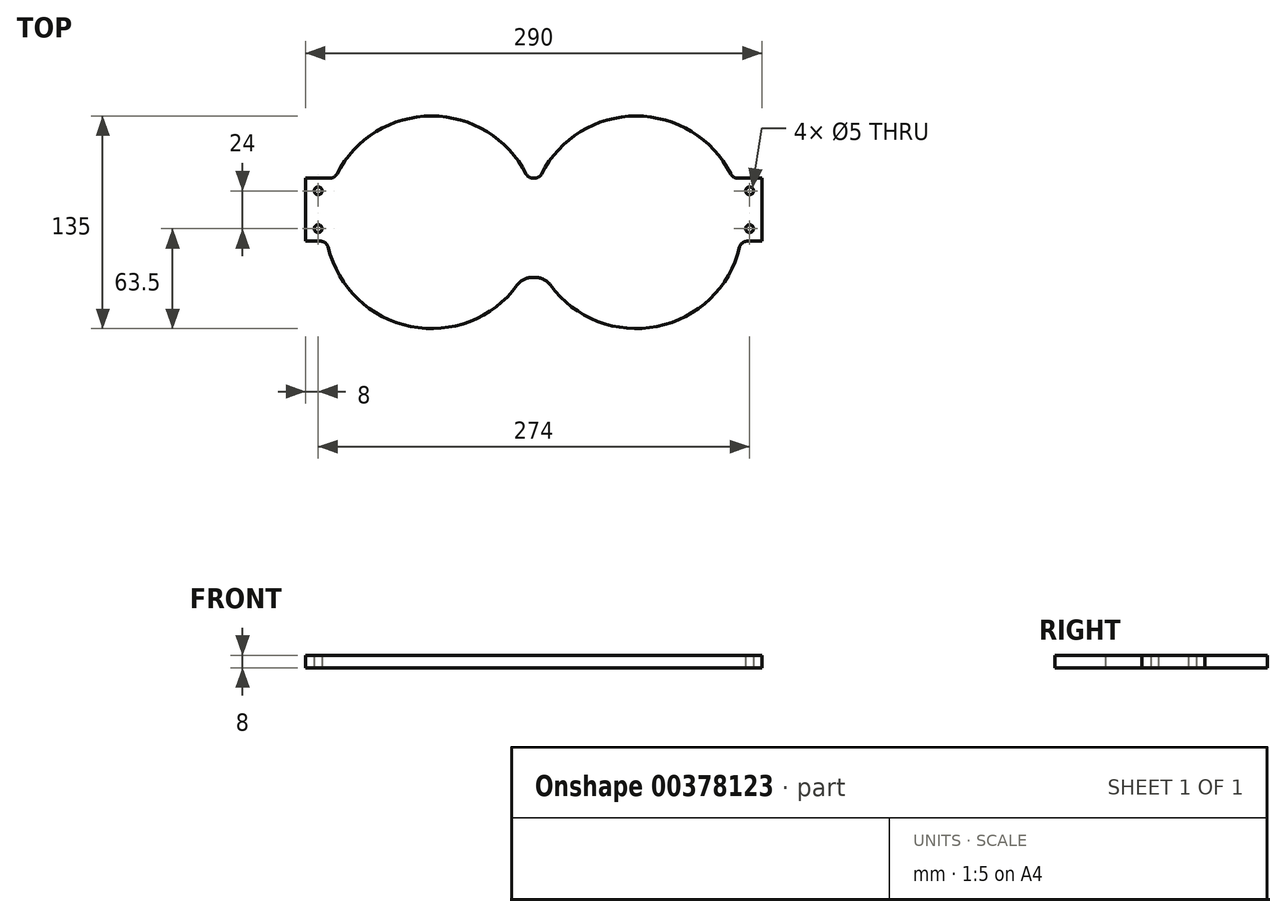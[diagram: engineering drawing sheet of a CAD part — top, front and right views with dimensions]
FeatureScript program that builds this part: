
annotation { "Feature Type Name" : "Feature", "Feature Type Description" : "" }
export const myFeature = defineFeature(function(context is Context, id is Id, definition is map)
    precondition{}
    {
        {
            var Q0;
            Q0=qCreatedBy(makeId("Top.planeOp"),FACE);
            var sketch = newSketch(context, id + "F0", { "sketchPlane" : qUnion([Q0])});
            skArc(sketch, "E0", {"start": v(7.28, -35) * mm, "mid": v(77.3, -66.37) * mm, "end": v(131.42, -12) * mm});
            skLineSegment(sketch, "E1", {"start": v(0, 0) * mm, "end": v(0, 28) * mm});
            skLineSegment(sketch, "E2", {"start": v(0, 28) * mm, "end": v(3.58, 28) * mm});
            skLineSegment(sketch, "E3", {"start": v(0, 0) * mm, "end": v(0, -35) * mm});
            skLineSegment(sketch, "E4", {"start": v(0, -35) * mm, "end": v(7.28, -35) * mm});
            skLineSegment(sketch, "E5", {"start": v(126.42, 28) * mm, "end": v(145, 28) * mm});
            skLineSegment(sketch, "E6", {"start": v(145, 28) * mm, "end": v(145, -12) * mm});
            skLineSegment(sketch, "E7", {"start": v(145, -12) * mm, "end": v(131.42, -12) * mm});
            skArc(sketch, "E8.trimOffspring", {"start": v(126.42, 28) * mm, "mid": v(65, 67.5) * mm, "end": v(3.58, 28) * mm});
            skCircle(sketch, "E9", {"center": v(137, 20) * mm, "radius": 2.5 * mm});
            skCircle(sketch, "E10", {"center": v(137, -4) * mm, "radius": 2.5 * mm});
            skSolve(sketch);
        }
        {
            var Q0;
            Q0=makeQuery(id+"F0.imprint","IMPRINT",FACE,{"disambiguationData":[TD([[makeQuery(id+"F0.imprint","IMPRINT",EDGE,{"derivedFrom":sQuery(id+"F0.wireOp",EDGE,"E0")}),1.0]])]});
            extrude(context, id + "F1", {"entities" : qUnion([Q0]), "depth" : 8 * mm});
        }
        {
            var Q0;
            Q0=makeQuery(id+"F1.opExtrude","SWEPT_BODY",BODY,{"disambiguationData":[OSD([sQuery(id+"F0.wireOp",EDGE,"E0"),sQuery(id+"F0.wireOp",EDGE,"E1"),sQuery(id+"F0.wireOp",EDGE,"E2"),sQuery(id+"F0.wireOp",EDGE,"E3"),sQuery(id+"F0.wireOp",EDGE,"E4"),sQuery(id+"F0.wireOp",EDGE,"E5"),sQuery(id+"F0.wireOp",EDGE,"E6"),sQuery(id+"F0.wireOp",EDGE,"E7"),sQuery(id+"F0.wireOp",EDGE,"E8.trimOffspring")])]});
            var Q1;
            Q1=makeQuery(id+"F1.opExtrude","SWEPT_FACE",FACE,{"disambiguationData":[OSD([sQuery(id+"F0.wireOp",EDGE,"E1"),sQuery(id+"F0.wireOp",EDGE,"E3")])]});
            mirror(context, id + "F2", {"operationType" : NewBodyOperationType.ADD, "entities" : qUnion([Q0]), "mirrorPlane" : qUnion([Q1])});
        }
        {
            var Q0;
            Q0=makeQuery(id+"F1.opExtrude","SWEPT_EDGE",EDGE,{"disambiguationData":[OSD([sQuery(id+"F0.wireOp",EDGE,"E0"),sQuery(id+"F0.wireOp",EDGE,"E4")])]});
            var Q1;
            Q1=makeQuery(id+"F2.opPattern","COPY",EDGE,{"derivedFrom":makeQuery(id+"F1.opExtrude","SWEPT_EDGE",EDGE,{"disambiguationData":[OSD([sQuery(id+"F0.wireOp",EDGE,"E0"),sQuery(id+"F0.wireOp",EDGE,"E4")])]}),"instanceName":"1"});
            fillet(context, id + "F3", {"entities" : qUnion([Q0, Q1]), "radius" : 12 * mm, "tangentPropagation" : true, "allowEdgeOverflow" : false});
        }
        {
            var Q0;
            Q0=makeQuery(id+"F1.opExtrude","SWEPT_EDGE",EDGE,{"disambiguationData":[OSD([sQuery(id+"F0.wireOp",EDGE,"E0"),sQuery(id+"F0.wireOp",EDGE,"E7")])]});
            var Q1;
            Q1=makeQuery(id+"F1.opExtrude","SWEPT_EDGE",EDGE,{"disambiguationData":[OSD([sQuery(id+"F0.wireOp",EDGE,"E5"),sQuery(id+"F0.wireOp",EDGE,"E8.trimOffspring")])]});
            var Q2;
            Q2=makeQuery(id+"F2.opPattern","COPY",EDGE,{"derivedFrom":makeQuery(id+"F1.opExtrude","SWEPT_EDGE",EDGE,{"disambiguationData":[OSD([sQuery(id+"F0.wireOp",EDGE,"E5"),sQuery(id+"F0.wireOp",EDGE,"E8.trimOffspring")])]}),"instanceName":"1"});
            var Q3;
            Q3=makeQuery(id+"F2.opPattern","COPY",EDGE,{"derivedFrom":makeQuery(id+"F1.opExtrude","SWEPT_EDGE",EDGE,{"disambiguationData":[OSD([sQuery(id+"F0.wireOp",EDGE,"E0"),sQuery(id+"F0.wireOp",EDGE,"E7")])]}),"instanceName":"1"});
            fillet(context, id + "F4", {"entities" : qUnion([Q0, Q1, Q2, Q3]), "radius" : 5 * mm, "tangentPropagation" : true, "allowEdgeOverflow" : false});
        }
        {
            var Q0;
            Q0=makeQuery(id+"F2.opPattern","COPY",EDGE,{"derivedFrom":makeQuery(id+"F1.opExtrude","SWEPT_EDGE",EDGE,{"disambiguationData":[OSD([sQuery(id+"F0.wireOp",EDGE,"E2"),sQuery(id+"F0.wireOp",EDGE,"E8.trimOffspring")])]}),"instanceName":"1"});
            var Q1;
            Q1=makeQuery(id+"F1.opExtrude","SWEPT_EDGE",EDGE,{"disambiguationData":[OSD([sQuery(id+"F0.wireOp",EDGE,"E2"),sQuery(id+"F0.wireOp",EDGE,"E8.trimOffspring")])]});
            fillet(context, id + "F5", {"entities" : qUnion([Q0, Q1]), "radius" : 5 * mm, "tangentPropagation" : true, "allowEdgeOverflow" : false});
        }
    });
